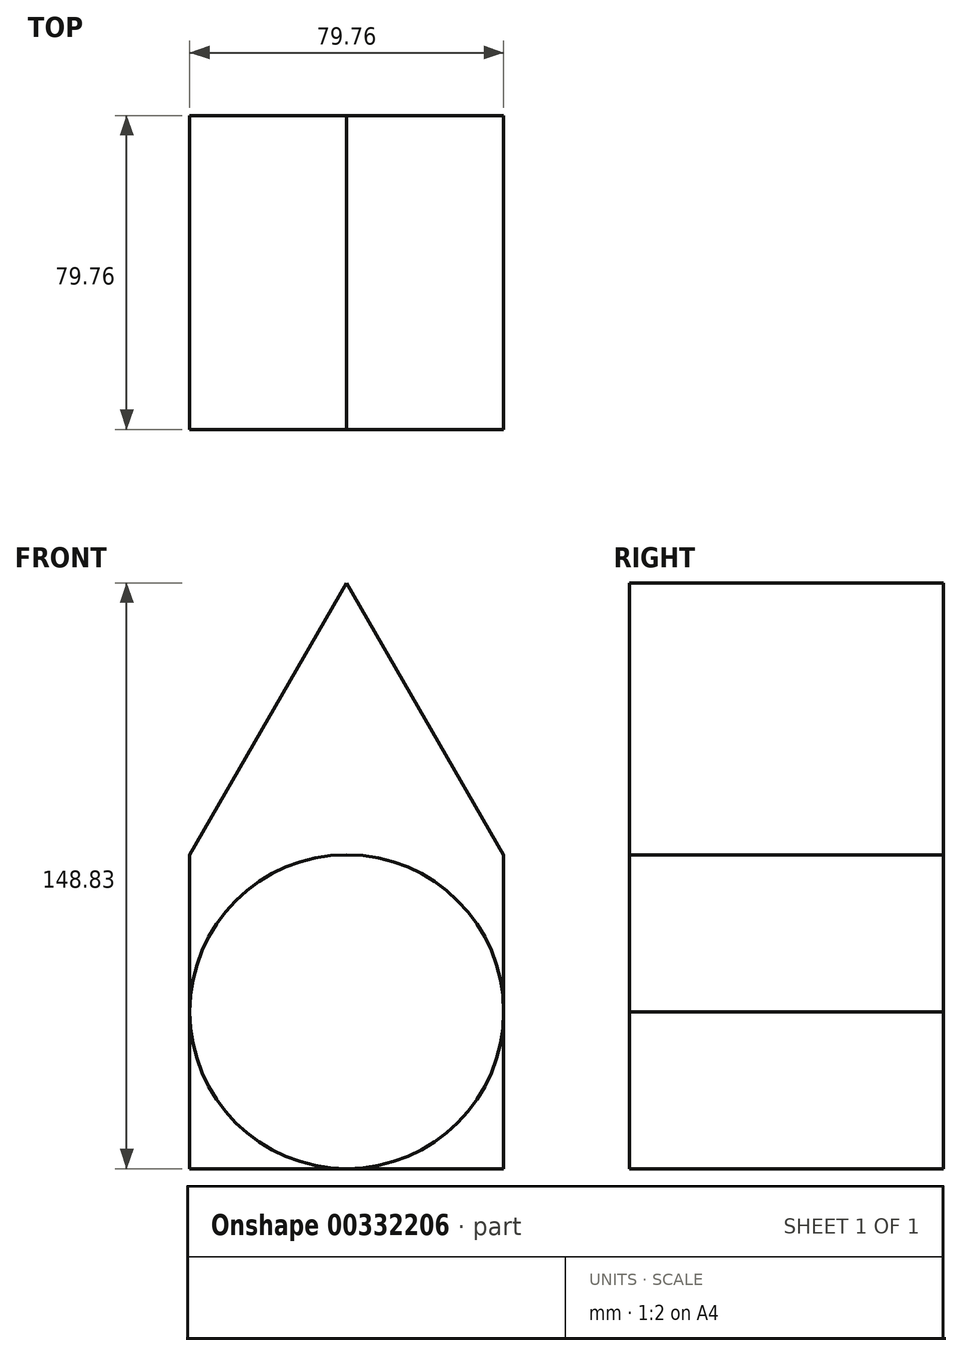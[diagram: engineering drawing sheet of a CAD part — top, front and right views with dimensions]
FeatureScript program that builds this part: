
annotation { "Feature Type Name" : "Feature", "Feature Type Description" : "" }
export const myFeature = defineFeature(function(context is Context, id is Id, definition is map)
    precondition{}
    {
        {
            var Q0;
            Q0=qCreatedBy(makeId("Front.planeOp"),FACE);
            var sketch = newSketch(context, id + "F0", { "sketchPlane" : qUnion([Q0])});
            skLineSegment(sketch, "E0.bottom", {"start": v(39.88, 39.88) * mm, "end": v(-39.88, 39.88) * mm});
            skLineSegment(sketch, "E0.top", {"start": v(39.88, -39.88) * mm, "end": v(-39.88, -39.88) * mm});
            skLineSegment(sketch, "E0.left", {"start": v(39.88, 39.88) * mm, "end": v(39.88, -39.88) * mm});
            skLineSegment(sketch, "E0.right", {"start": v(-39.88, 39.88) * mm, "end": v(-39.88, -39.88) * mm});
            skPoint(sketch, "E0.middle", {"position": v(0, 0) * mm});
            skCircle(sketch, "E1", {"center": v(0, 0) * mm, "radius": 39.88 * mm});
            skLineSegment(sketch, "E2", {"start": v(-39.88, 39.88) * mm, "end": v(0, 108.95) * mm});
            skLineSegment(sketch, "E3", {"start": v(0, 108.95) * mm, "end": v(39.88, 39.88) * mm});
            skSolve(sketch);
        }
        {
            var Q0;
            {var subQ0=sQuery(id+"F0.wireOp",EDGE,"E0.right");var subQ3=sQuery(id+"F0.wireOp",EDGE,"E1");var subQ5=makeQuery(id+"F0.imprint","INTERSECT",VERTEX,{"derivedFrom":[subQ0,subQ3]});Q0=makeQuery(id+"F0.imprint","IMPRINT",FACE,{"disambiguationData":[TD([[makeQuery(id+"F0.imprint","IMPRINT",EDGE,{"disambiguationData":[TD([[subQ5,1.0]])],"derivedFrom":subQ3}),-1.0]])]});}
            var Q1;
            {var subQ3=sQuery(id+"F0.wireOp",EDGE,"E2");Q1=makeQuery(id+"F0.imprint","IMPRINT",FACE,{"disambiguationData":[TD([[makeQuery(id+"F0.imprint","IMPRINT",EDGE,{"derivedFrom":subQ3}),-1.0]])]});}
            var Q2;
            {var subQ0=sQuery(id+"F0.wireOp",EDGE,"E0.left");var subQ3=sQuery(id+"F0.wireOp",EDGE,"E1");var subQ5=makeQuery(id+"F0.imprint","INTERSECT",VERTEX,{"derivedFrom":[subQ0,subQ3]});Q2=makeQuery(id+"F0.imprint","IMPRINT",FACE,{"disambiguationData":[TD([[makeQuery(id+"F0.imprint","IMPRINT",EDGE,{"disambiguationData":[TD([[subQ5,-1.0]])],"derivedFrom":subQ3}),-1.0]])]});}
            var Q3;
            {var subQ0=sQuery(id+"F0.wireOp",EDGE,"E0.left");var subQ1=sQuery(id+"F0.wireOp",EDGE,"E0.top");var subQ2=makeQuery(id+"F0.imprint","INTERSECT",VERTEX,{"derivedFrom":[subQ1,subQ0]});Q3=makeQuery(id+"F0.imprint","IMPRINT",FACE,{"disambiguationData":[TD([[makeQuery(id+"F0.imprint","IMPRINT",EDGE,{"disambiguationData":[TD([[subQ2,-1.0]])],"derivedFrom":subQ1}),-1.0]])]});}
            var Q4;
            {var subQ0=sQuery(id+"F0.wireOp",EDGE,"E0.right");var subQ1=sQuery(id+"F0.wireOp",EDGE,"E0.top");var subQ2=makeQuery(id+"F0.imprint","INTERSECT",VERTEX,{"derivedFrom":[subQ1,subQ0]});Q4=makeQuery(id+"F0.imprint","IMPRINT",FACE,{"disambiguationData":[TD([[makeQuery(id+"F0.imprint","IMPRINT",EDGE,{"disambiguationData":[TD([[subQ2,1.0]])],"derivedFrom":subQ1}),-1.0]])]});}
            extrude(context, id + "F1", {"entities" : qUnion([Q0, Q1, Q2, Q3, Q4]), "depth" : 79.76 * mm});
        }
    });
